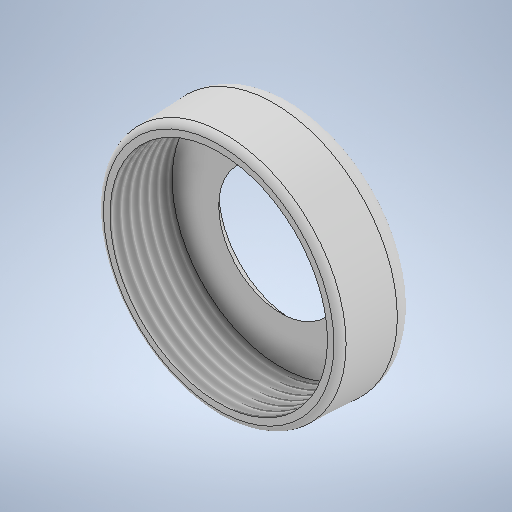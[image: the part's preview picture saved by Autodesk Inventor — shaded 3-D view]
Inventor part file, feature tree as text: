
AUTODESK INVENTOR PART (.ipt)
format: ipt  version: 2025.1 (Build 291241000, 241)  size: 325,120 bytes
history: native  units: mm
features: fillet x2, revolve x1, chamfer x1, thread x1, sketch x1
ambient origin geometry x8: Origin, YZ Plane, XZ Plane, XY Plane, X Axis, Y Axis, Z Axis, Center Point
bodies: Volumenkörper1 (feature_tree)
feature tree (6):
  revolve  "Umdrehung1"
  chamfer  "Fasen1"  Distance=10.0mm
  thread  "Gewinde1"  [1 undecoded]
  fillet  "Rundung1"  Radius=2.0mm
  fillet  "Rundung2"  [1 undecoded]
  sketch  "Skizze1"  dims[d0=35.0mm d1=10.0mm d2=20.0mm d4=2.0mm d5=90.0deg d6=2.0mm d7=2.0mm d8=45.0deg d9=10.0mm d10=2.0mm d11=16.0mm d12=0.0mm d13=3.0mm d14=1.0mm d15=1.0mm d16=1.5mm d17=0.872665mm d18=0.872665mm]
note: 2 required parameter values undecoded (feature->parameter linkage not recoverable at this tier; creation-order binding heuristic only, values carry confidence <= 0.55)
